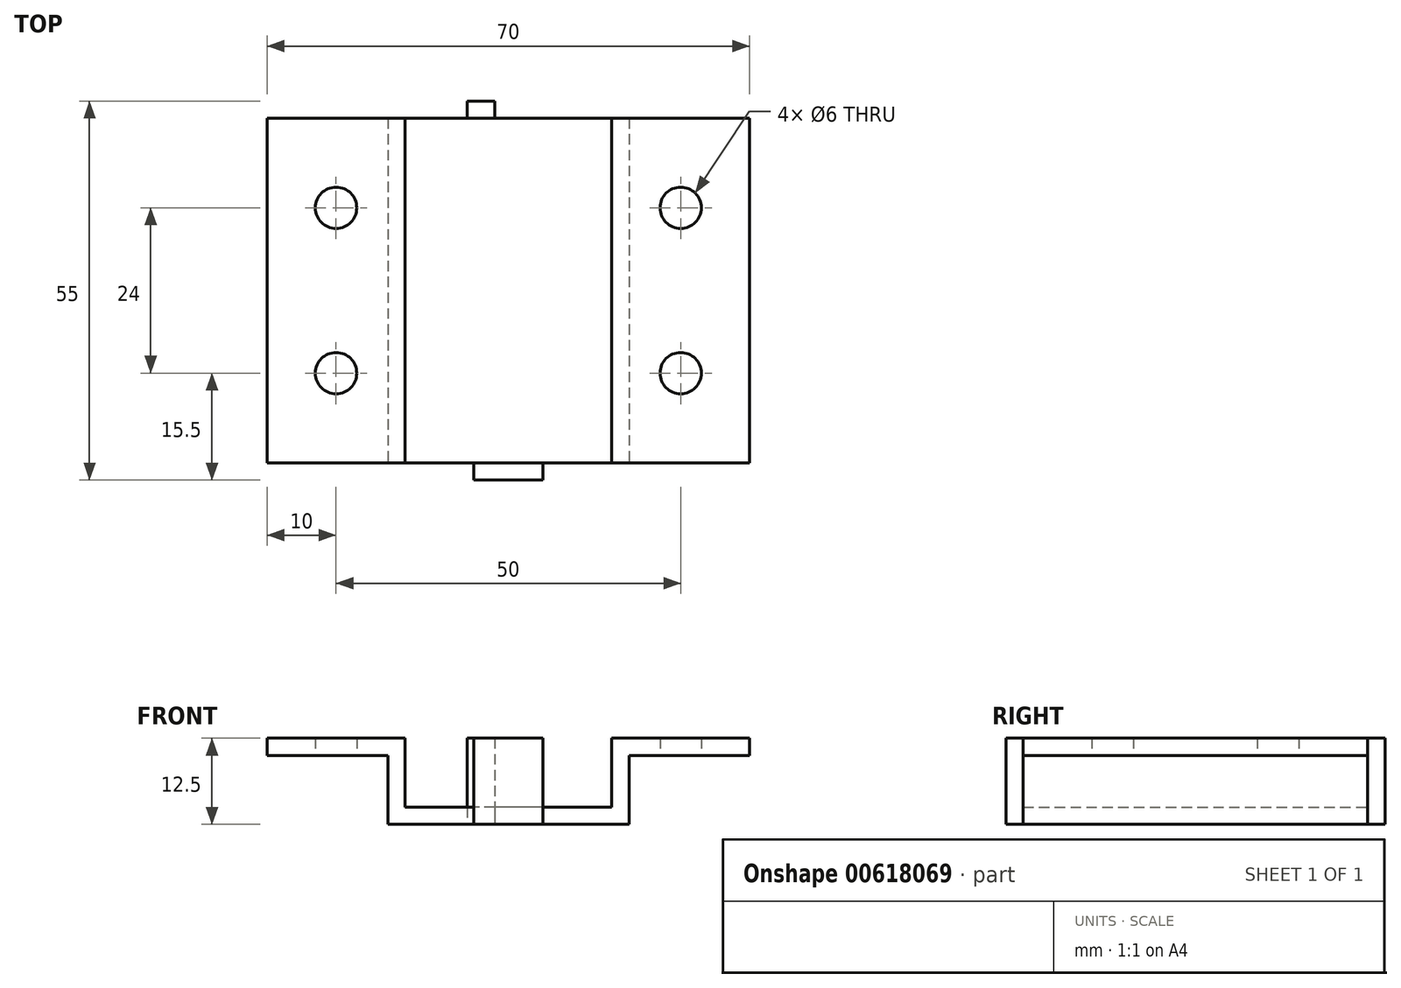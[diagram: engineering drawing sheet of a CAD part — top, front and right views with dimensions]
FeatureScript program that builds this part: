
annotation { "Feature Type Name" : "Feature", "Feature Type Description" : "" }
export const myFeature = defineFeature(function(context is Context, id is Id, definition is map)
    precondition{}
    {
        {
            var Q0;
            Q0=qCreatedBy(makeId("Top.planeOp"),FACE);
            var sketch = newSketch(context, id + "F0", { "sketchPlane" : qUnion([Q0])});
            skLineSegment(sketch, "E0.bottom", {"start": v(15, -24.13) * mm, "end": v(-15, -24.13) * mm});
            skLineSegment(sketch, "E0.top", {"start": v(15, 25.87) * mm, "end": v(-15, 25.87) * mm});
            skLineSegment(sketch, "E0.left", {"start": v(15, -24.13) * mm, "end": v(15, 25.87) * mm});
            skLineSegment(sketch, "E0.right", {"start": v(-15, -24.13) * mm, "end": v(-15, 25.87) * mm});
            skPoint(sketch, "E0.middle", {"position": v(0, 0.87) * mm});
            skSolve(sketch);
        }
        {
            var Q0;
            Q0 = qSketchRegion(id + "F0", true);
            extrude(context, id + "F1", {"entities" : qUnion([Q0]), "depth" : 2.5 * mm, "offsetDistance" : 25 * mm});
        }
        {
            var Q0;
            Q0=qCreatedBy(makeId("Top.planeOp"),FACE);
            var sketch = newSketch(context, id + "F2", { "sketchPlane" : qUnion([Q0])});
            skLineSegment(sketch, "E1.0", {"start": v(15, -24.13) * mm, "end": v(15, 25.87) * mm});
            skLineSegment(sketch, "E2.0", {"start": v(-15, -24.13) * mm, "end": v(-15, 25.87) * mm});
            skLineSegment(sketch, "E3.bottom", {"start": v(15, 25.87) * mm, "end": v(17.5, 25.87) * mm});
            skLineSegment(sketch, "E3.top", {"start": v(15, -24.13) * mm, "end": v(17.5, -24.13) * mm});
            skLineSegment(sketch, "E3.left", {"start": v(15, 25.87) * mm, "end": v(15, -24.13) * mm});
            skLineSegment(sketch, "E3.right", {"start": v(17.5, 25.87) * mm, "end": v(17.5, -24.13) * mm});
            skLineSegment(sketch, "E4.MirrorCS", {"start": v(-15, -24.13) * mm, "end": v(-17.5, -24.13) * mm});
            skLineSegment(sketch, "E5.MirrorCS", {"start": v(-15, 25.87) * mm, "end": v(-15, -24.13) * mm});
            skLineSegment(sketch, "E6.MirrorCS", {"start": v(-17.5, 25.87) * mm, "end": v(-17.5, -24.13) * mm});
            skLineSegment(sketch, "E7.MirrorCS", {"start": v(-15, 25.87) * mm, "end": v(-17.5, 25.87) * mm});
            skSolve(sketch);
        }
        {
            var Q0;
            Q0 = qSketchRegion(id + "F2", true);
            extrude(context, id + "F3", {"entities" : qUnion([Q0]), "operationType" : NewBodyOperationType.ADD, "depth" : 10 * mm, "offsetDistance" : 25 * mm});
        }
        {
            var Q0;
            Q0=makeQuery(id+"F3.opExtrude","CAP_FACE",FACE,{"disambiguationData":[OSD([sQuery(id+"F2.wireOp",EDGE,"E3.bottom"),sQuery(id+"F2.wireOp",EDGE,"E3.top"),sQuery(id+"F2.wireOp",EDGE,"E3.left"),sQuery(id+"F2.wireOp",EDGE,"E3.right")])],"isStart":false});
            var sketch = newSketch(context, id + "F4", { "sketchPlane" : qUnion([Q0])});
            skLineSegment(sketch, "E8.bottom", {"start": v(15, 25.87) * mm, "end": v(35, 25.87) * mm});
            skLineSegment(sketch, "E8.top", {"start": v(15, -24.13) * mm, "end": v(35, -24.13) * mm});
            skLineSegment(sketch, "E8.left", {"start": v(15, 25.87) * mm, "end": v(15, -24.13) * mm});
            skLineSegment(sketch, "E8.right", {"start": v(35, 25.87) * mm, "end": v(35, -24.13) * mm});
            skLineSegment(sketch, "E9", {"start": v(25, 25.87) * mm, "end": v(25, -24.13) * mm, "construction": true});
            skCircle(sketch, "E10", {"center": v(25, 12.87) * mm, "radius": 3 * mm});
            skCircle(sketch, "E11", {"center": v(25, -11.13) * mm, "radius": 3 * mm});
            skLineSegment(sketch, "E12.MirrorCS", {"start": v(35, -24.13) * mm, "end": v(15, -24.13) * mm});
            skLineSegment(sketch, "E13.MirrorCS", {"start": v(35, 25.87) * mm, "end": v(15, 25.87) * mm});
            skLineSegment(sketch, "E14.MirrorCS", {"start": v(-15, 25.87) * mm, "end": v(-15, -24.13) * mm});
            skCircle(sketch, "E15.MirrorC", {"center": v(-25, 12.87) * mm, "radius": 3 * mm});
            skLineSegment(sketch, "E16.MirrorCS", {"start": v(-15, 25.87) * mm, "end": v(-35, 25.87) * mm});
            skLineSegment(sketch, "E17.MirrorCS", {"start": v(-15, -24.13) * mm, "end": v(-35, -24.13) * mm});
            skLineSegment(sketch, "E18.MirrorCS", {"start": v(-35, 25.87) * mm, "end": v(-35, -24.13) * mm});
            skCircle(sketch, "E19.MirrorC", {"center": v(-25, -11.13) * mm, "radius": 3 * mm});
            skLineSegment(sketch, "E20.MirrorCS", {"start": v(-35, 25.87) * mm, "end": v(-15, 25.87) * mm});
            skLineSegment(sketch, "E21.MirrorCS", {"start": v(-35, -24.13) * mm, "end": v(-15, -24.13) * mm});
            skLineSegment(sketch, "E22.MirrorCS", {"start": v(-25, 25.87) * mm, "end": v(-25, -24.13) * mm, "construction": true});
            skSolve(sketch);
        }
        {
            var Q0;
            Q0 = qSketchRegion(id + "F4", true);
            extrude(context, id + "F5", {"entities" : qUnion([Q0]), "operationType" : NewBodyOperationType.ADD, "depth" : 2.5 * mm, "offsetDistance" : 25 * mm});
        }
        {
            var Q0;
            Q0=qCreatedBy(makeId("Top.planeOp"),FACE);
            var sketch = newSketch(context, id + "F6", { "sketchPlane" : qUnion([Q0])});
            skLineSegment(sketch, "E23.bottom", {"start": v(-6, 25.87) * mm, "end": v(-2, 25.87) * mm});
            skLineSegment(sketch, "E23.top", {"start": v(-6, 28.37) * mm, "end": v(-2, 28.37) * mm});
            skLineSegment(sketch, "E23.left", {"start": v(-6, 25.87) * mm, "end": v(-6, 28.37) * mm});
            skLineSegment(sketch, "E23.right", {"start": v(-2, 25.87) * mm, "end": v(-2, 28.37) * mm});
            skSolve(sketch);
        }
        {
            var Q0;
            Q0 = qSketchRegion(id + "F6", true);
            var Q1;
            Q1=makeQuery(id+"F5.opExtrude","CAP_FACE",FACE,{"disambiguationData":[OSD([sQuery(id+"F4.wireOp",EDGE,"E21.MirrorCS"),sQuery(id+"F4.wireOp",EDGE,"E18.MirrorCS"),sQuery(id+"F4.wireOp",EDGE,"E15.MirrorC"),sQuery(id+"F4.wireOp",EDGE,"E20.MirrorCS"),sQuery(id+"F4.wireOp",EDGE,"E19.MirrorC"),sQuery(id+"F4.wireOp",EDGE,"E14.MirrorCS")])],"isStart":false});
            extrude(context, id + "F7", {"entities" : qUnion([Q0]), "operationType" : NewBodyOperationType.ADD, "endBound" : BoundingType.UP_TO_SURFACE, "depth" : 7.5 * mm, "endBoundEntityFace" : qUnion([Q1]), "offsetDistance" : 25 * mm});
        }
        {
            var Q0;
            Q0=qCreatedBy(makeId("Top.planeOp"),FACE);
            var sketch = newSketch(context, id + "F8", { "sketchPlane" : qUnion([Q0])});
            skLineSegment(sketch, "E24.0", {"start": v(15, -24.13) * mm, "end": v(-15, -24.13) * mm});
            skLineSegment(sketch, "E25.bottom", {"start": v(-5, -24.13) * mm, "end": v(5, -24.13) * mm});
            skLineSegment(sketch, "E25.top", {"start": v(-5, -26.63) * mm, "end": v(5, -26.63) * mm});
            skLineSegment(sketch, "E25.left", {"start": v(-5, -24.13) * mm, "end": v(-5, -26.63) * mm});
            skLineSegment(sketch, "E25.right", {"start": v(5, -24.13) * mm, "end": v(5, -26.63) * mm});
            skPoint(sketch, "E26", {"position": v(0, -26.63) * mm});
            skSolve(sketch);
        }
        {
            var Q0;
            Q0 = qSketchRegion(id + "F8", true);
            var Q1;
            Q1=makeQuery(id+"F5.opExtrude","CAP_FACE",FACE,{"disambiguationData":[OSD([sQuery(id+"F4.wireOp",EDGE,"E21.MirrorCS"),sQuery(id+"F4.wireOp",EDGE,"E18.MirrorCS"),sQuery(id+"F4.wireOp",EDGE,"E15.MirrorC"),sQuery(id+"F4.wireOp",EDGE,"E20.MirrorCS"),sQuery(id+"F4.wireOp",EDGE,"E19.MirrorC"),sQuery(id+"F4.wireOp",EDGE,"E14.MirrorCS")])],"isStart":false});
            extrude(context, id + "F9", {"entities" : qUnion([Q0]), "operationType" : NewBodyOperationType.ADD, "endBound" : BoundingType.UP_TO_SURFACE, "depth" : 7.5 * mm, "endBoundEntityFace" : qUnion([Q1]), "offsetDistance" : 25 * mm});
        }
    });
